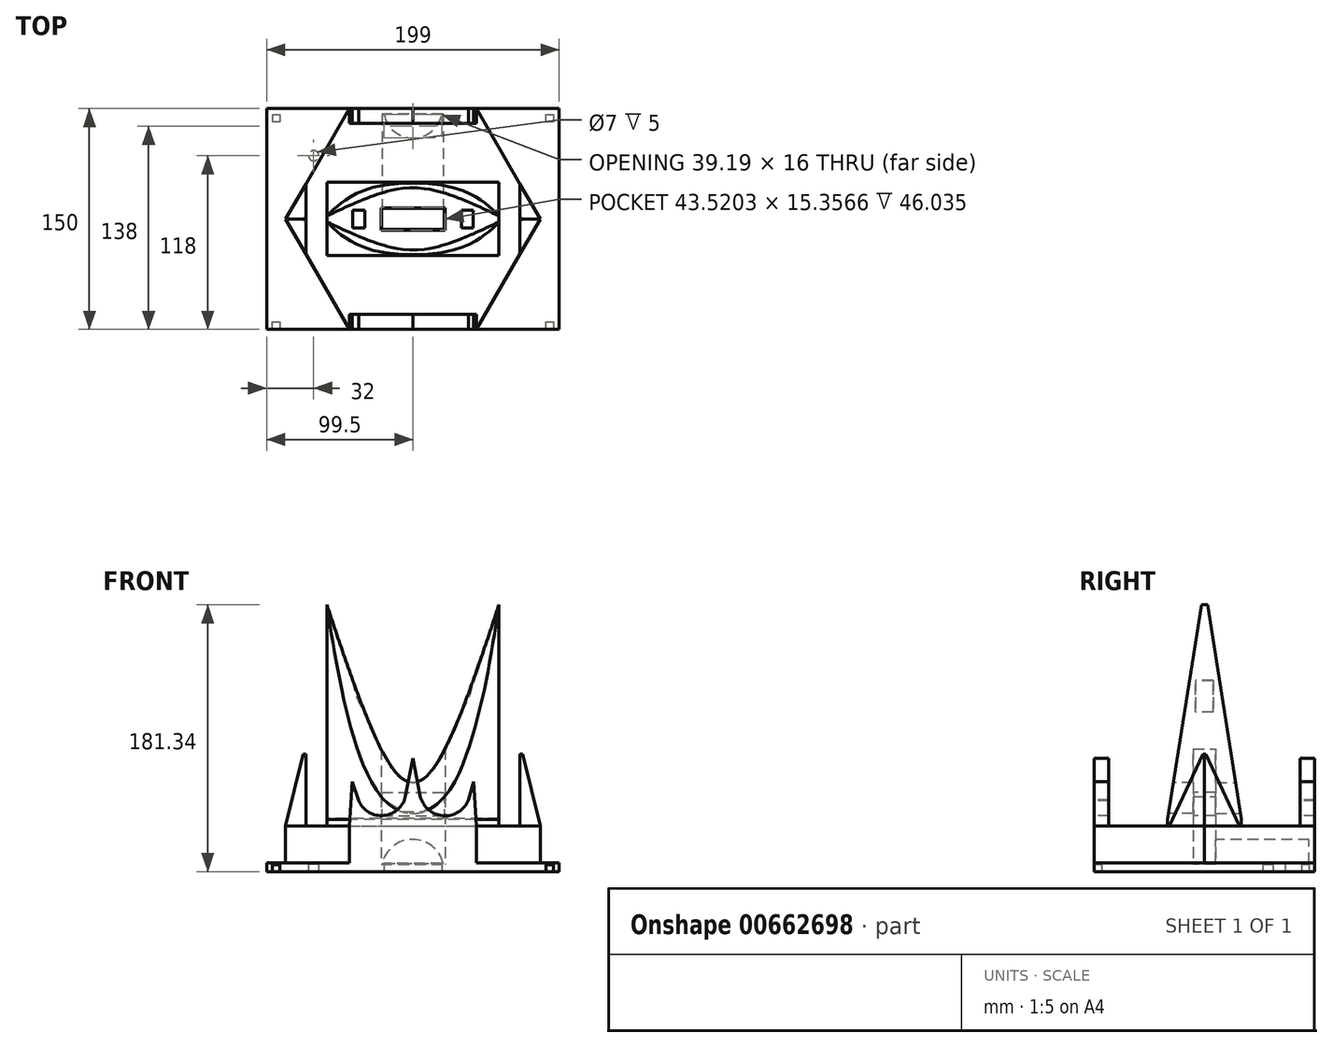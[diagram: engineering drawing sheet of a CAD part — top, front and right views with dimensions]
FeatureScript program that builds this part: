
annotation { "Feature Type Name" : "Feature", "Feature Type Description" : "" }
export const myFeature = defineFeature(function(context is Context, id is Id, definition is map)
    precondition{}
    {
        {
            var Q0;
            Q0=qCreatedBy(makeId("Top.planeOp"),FACE);
            var sketch = newSketch(context, id + "F0", { "sketchPlane" : qUnion([Q0])});
            skLineSegment(sketch, "E0.bottom", {"start": v(-99.5, 75) * mm, "end": v(99.5, 75) * mm});
            skLineSegment(sketch, "E0.left", {"start": v(-99.5, 75) * mm, "end": v(-99.5, -75) * mm});
            skLineSegment(sketch, "E0.right", {"start": v(99.5, 75) * mm, "end": v(99.5, -75) * mm});
            skPoint(sketch, "E0.middle", {"position": v(0, 0) * mm});
            skLineSegment(sketch, "E1.1", {"start": v(-95.5, 71) * mm, "end": v(-95.5, -70) * mm});
            skLineSegment(sketch, "E1.2", {"start": v(-95.5, 71) * mm, "end": v(95.4, 71) * mm});
            skLineSegment(sketch, "E1.3", {"start": v(95.4, 71) * mm, "end": v(95.4, -70) * mm});
            skLineSegment(sketch, "E2", {"start": v(0, -75) * mm, "end": v(0, -73) * mm});
            skPoint(sketch, "E2.endSnap0", {"position": v(0, -75) * mm});
            skPoint(sketch, "E3.end.orphan", {"position": v(95.5, 0) * mm});
            skLineSegment(sketch, "E4", {"start": v(-99.5, -75) * mm, "end": v(-95.5, -75) * mm});
            skLineSegment(sketch, "E5", {"start": v(-95.5, -75) * mm, "end": v(-95.5, -70) * mm});
            skLineSegment(sketch, "E6", {"start": v(95.4, -70) * mm, "end": v(95.4, -75) * mm});
            skLineSegment(sketch, "E7", {"start": v(95.4, -75) * mm, "end": v(99.5, -75) * mm});
            skPoint(sketch, "E8.end.orphan", {"position": v(-95.5, -70) * mm});
            skLineSegment(sketch, "E9", {"start": v(-90.5, 71) * mm, "end": v(-90.5, 66) * mm});
            skLineSegment(sketch, "E10", {"start": v(-90.5, 66) * mm, "end": v(-95.5, 66) * mm});
            skLineSegment(sketch, "E11", {"start": v(95.4, 66) * mm, "end": v(90.4, 66) * mm});
            skLineSegment(sketch, "E12", {"start": v(90.4, 66) * mm, "end": v(90.4, 71) * mm});
            skLineSegment(sketch, "E13", {"start": v(-95.5, 71) * mm, "end": v(-90.5, 71) * mm});
            skLineSegment(sketch, "E14", {"start": v(-95.5, 71) * mm, "end": v(-95.5, 66) * mm});
            skLineSegment(sketch, "E15", {"start": v(90.4, 71) * mm, "end": v(95.4, 71) * mm});
            skLineSegment(sketch, "E16", {"start": v(95.4, 66) * mm, "end": v(95.4, 71) * mm});
            skLineSegment(sketch, "E17", {"start": v(95.4, -75) * mm, "end": v(90.4, -75) * mm});
            skLineSegment(sketch, "E18", {"start": v(90.4, -75) * mm, "end": v(90.4, -70) * mm});
            skLineSegment(sketch, "E19", {"start": v(90.4, -70) * mm, "end": v(95.4, -70) * mm});
            skLineSegment(sketch, "E20", {"start": v(-95.5, -70) * mm, "end": v(-90.5, -70) * mm});
            skLineSegment(sketch, "E21", {"start": v(-95.5, -75) * mm, "end": v(-90.5, -75) * mm});
            skLineSegment(sketch, "E22", {"start": v(-90.5, -70) * mm, "end": v(-90.5, -75) * mm});
            skLineSegment(sketch, "E23", {"start": v(0, 73) * mm, "end": v(0, 71) * mm});
            skPoint(sketch, "E24.MirrorCS.end.orphan", {"position": v(-8.62, 71) * mm});
            skPoint(sketch, "E24.MirrorCS.start.orphan", {"position": v(8.62, 71) * mm});
            skSolve(sketch);
        }
        {
            var Q0;
            Q0=qCreatedBy(makeId("Top.planeOp"),FACE);
            var sketch = newSketch(context, id + "F1", { "sketchPlane" : qUnion([Q0])});
            skLineSegment(sketch, "E25.bottom", {"start": v(-99.5, 75) * mm, "end": v(-20, 75) * mm});
            skLineSegment(sketch, "E25.top", {"start": v(-99.5, -75) * mm, "end": v(99.5, -75) * mm});
            skLineSegment(sketch, "E25.left", {"start": v(-99.5, 75) * mm, "end": v(-99.5, -75) * mm});
            skLineSegment(sketch, "E25.right", {"start": v(99.5, 75) * mm, "end": v(99.5, -75) * mm});
            skPoint(sketch, "E25.middle", {"position": v(0, 0) * mm});
            skCircle(sketch, "E26", {"center": v(-67.5, 43) * mm, "radius": 3.5 * mm});
            skLineSegment(sketch, "E27.trimOffspring", {"start": v(20, 75) * mm, "end": v(99.5, 75) * mm});
            skArc(sketch, "E28", {"start": v(-20, 75) * mm, "mid": v(0, 55) * mm, "end": v(20, 75) * mm});
            skLineSegment(sketch, "E29", {"start": v(-20, 75) * mm, "end": v(20, 75) * mm});
            skLineSegment(sketch, "E30", {"start": v(19.6, 71) * mm, "end": v(-19.6, 71) * mm});
            skLineSegment(sketch, "E31", {"start": v(-67.5, 43) * mm, "end": v(-67.5, 75) * mm});
            skLineSegment(sketch, "E32", {"start": v(-67.5, 43) * mm, "end": v(-99.5, 43) * mm});
            skSolve(sketch);
        }
        {
            var Q0;
            Q0=qSketchRegion(id+"F1",true);
            extrude(context, id + "F2", {"entities" : qUnion([Q0]), "depth" : 6 * mm, "offsetDistance" : 25 * mm});
        }
        {
            var Q0;
            Q0=makeQuery(id+"F0.imprint","IMPRINT",FACE,{"disambiguationData":[TD([[makeQuery(id+"F0.imprint","IMPRINT",EDGE,{"derivedFrom":sQuery(id+"F0.wireOp",EDGE,"E9")}),-1.0]])]});
            var Q1;
            Q1=makeQuery(id+"F0.imprint","IMPRINT",FACE,{"disambiguationData":[TD([[makeQuery(id+"F0.imprint","IMPRINT",EDGE,{"derivedFrom":sQuery(id+"F0.wireOp",EDGE,"E11")}),-1.0]])]});
            var Q2;
            Q2=makeQuery(id+"F0.imprint","IMPRINT",FACE,{"disambiguationData":[TD([[makeQuery(id+"F0.imprint","IMPRINT",EDGE,{"derivedFrom":sQuery(id+"F0.wireOp",EDGE,"E5")}),-1.0]])]});
            var Q3;
            Q3=makeQuery(id+"F0.imprint","IMPRINT",FACE,{"disambiguationData":[TD([[makeQuery(id+"F0.imprint","IMPRINT",EDGE,{"derivedFrom":sQuery(id+"F0.wireOp",EDGE,"E6")}),-1.0]])]});
            extrude(context, id + "F3", {"entities" : qUnion([Q0, Q1, Q2, Q3]), "operationType" : NewBodyOperationType.REMOVE, "depth" : 4.5 * mm, "offsetDistance" : 25 * mm});
        }
        {
            var Q0;
            Q0=makeQuery(id+"F2.opExtrude","CAP_FACE",FACE,{"disambiguationData":[OSD([sQuery(id+"F1.wireOp",EDGE,"E25.bottom"),sQuery(id+"F1.wireOp",EDGE,"E25.top"),sQuery(id+"F1.wireOp",EDGE,"E25.left"),sQuery(id+"F1.wireOp",EDGE,"E25.right"),sQuery(id+"F1.wireOp",EDGE,"E26"),sQuery(id+"F1.wireOp",EDGE,"E27.trimOffspring"),sQuery(id+"F1.wireOp",EDGE,"E28")])],"isStart":false});
            var sketch = newSketch(context, id + "F4", { "sketchPlane" : qUnion([Q0])});
            skCircle(sketch, "E33.cCircle", {"center": v(0, 0) * mm, "radius": 75 * mm, "construction": true});
            skLineSegment(sketch, "E33.0", {"start": v(-43.3, 75) * mm, "end": v(43.3, 75) * mm});
            skLineSegment(sketch, "E33.1", {"start": v(43.3, 75) * mm, "end": v(86.6, 0) * mm});
            skLineSegment(sketch, "E33.2", {"start": v(86.6, 0) * mm, "end": v(43.3, -75) * mm});
            skLineSegment(sketch, "E33.3", {"start": v(43.3, -75) * mm, "end": v(-43.3, -75) * mm});
            skLineSegment(sketch, "E33.4", {"start": v(-43.3, -75) * mm, "end": v(-86.6, 0) * mm});
            skLineSegment(sketch, "E33.5", {"start": v(-86.6, 0) * mm, "end": v(-43.3, 75) * mm});
            skPoint(sketch, "E33.0.midPoint", {"position": v(0, 75) * mm});
            skCircle(sketch, "E34", {"center": v(-67.5, 43) * mm, "radius": 3.84 * mm});
            skSolve(sketch);
        }
        {
            var Q0;
            Q0=makeQuery(id+"F4.imprint","IMPRINT",FACE,{"disambiguationData":[TD([[makeQuery(id+"F4.imprint","IMPRINT",EDGE,{"derivedFrom":makeQuery(id+"F2.opExtrude","CAP_EDGE",EDGE,{"disambiguationData":[OSD([sQuery(id+"F1.wireOp",EDGE,"E26")])],"isStart":false})}),1.0]])]});
            extrude(context, id + "F5", {"entities" : qUnion([Q0]), "operationType" : NewBodyOperationType.ADD, "oppositeDirection" : true, "depth" : 1 * mm, "offsetDistance" : 25 * mm});
        }
        {
            var Q0;
            {var subQ0=sQuery(id+"F4.wireOp",EDGE,"E33.1");Q0=makeQuery(id+"F4.imprint","IMPRINT",FACE,{"disambiguationData":[TD([[makeQuery(id+"F4.imprint","IMPRINT",EDGE,{"derivedFrom":subQ0}),-1.0]])]});}
            var Q1;
            {var subQ1=makeQuery(id+"F2.opExtrude","CAP_EDGE",EDGE,{"disambiguationData":[OSD([sQuery(id+"F1.wireOp",EDGE,"E28")])],"isStart":false});Q1=makeQuery(id+"F4.imprint","IMPRINT",FACE,{"disambiguationData":[TD([[makeQuery(id+"F4.imprint","IMPRINT",EDGE,{"derivedFrom":subQ1}),1.0]])]});}
            extrude(context, id + "F6", {"entities" : qUnion([Q0, Q1]), "operationType" : NewBodyOperationType.ADD, "depth" : 25 * mm, "offsetDistance" : 25 * mm});
        }
        {
            var Q0;
            Q0=makeQuery(id+"F6.boolean.opBoolean","MERGE",FACE,{"derivedFrom":[makeQuery(id+"F2.opExtrude","SWEPT_FACE",FACE,{"disambiguationData":[OSD([sQuery(id+"F1.wireOp",EDGE,"E25.top")])]}),makeQuery(id+"F6.opExtrude","SWEPT_FACE",FACE,{"disambiguationData":[OSD([sQuery(id+"F4.wireOp",EDGE,"E33.3")])]})]});
            var sketch = newSketch(context, id + "F7", { "sketchPlane" : qUnion([Q0])});
            skLineSegment(sketch, "E35", {"start": v(-43.3, 31) * mm, "end": v(43.3, 31) * mm});
            skLineSegment(sketch, "E36", {"start": v(-41.3, 61) * mm, "end": v(-43.3, 31) * mm});
            skLineSegment(sketch, "E37", {"start": v(-36.89, 48.16) * mm, "end": v(-41.3, 61) * mm});
            skLineSegment(sketch, "E38", {"start": v(4.9, 51.85) * mm, "end": v(-0.01, 77) * mm});
            skLineSegment(sketch, "E39", {"start": v(-4.94, 51.67) * mm, "end": v(-0.01, 77) * mm});
            skLineSegment(sketch, "E40", {"start": v(41.3, 61) * mm, "end": v(37.86, 48.79) * mm});
            skLineSegment(sketch, "E41", {"start": v(43.3, 31) * mm, "end": v(41.3, 61) * mm});
            skArc(sketch, "E42", {"start": v(-36.89, 48.16) * mm, "mid": v(-19.62, 38.15) * mm, "end": v(-4.94, 51.67) * mm});
            skArc(sketch, "E43", {"start": v(4.9, 51.85) * mm, "mid": v(20.24, 37.98) * mm, "end": v(37.86, 48.79) * mm});
            skSolve(sketch);
        }
        {
            var Q0;
            Q0=makeQuery(id+"F7.imprint","IMPRINT",FACE,{"disambiguationData":[TD([[makeQuery(id+"F7.imprint","IMPRINT",EDGE,{"derivedFrom":sQuery(id+"F7.wireOp",EDGE,"E35")}),1.0]])]});
            extrude(context, id + "F8", {"entities" : qUnion([Q0]), "operationType" : NewBodyOperationType.ADD, "oppositeDirection" : true, "depth" : 10 * mm, "offsetDistance" : 25 * mm});
        }
        {
            var Q0;
            {var subQ0=sQuery(id+"F4.wireOp",EDGE,"E33.1");var subQ1=sQuery(id+"F4.wireOp",EDGE,"E33.0");var subQ3=sQuery(id+"F4.wireOp",EDGE,"E33.2");var subQ4=sQuery(id+"F4.wireOp",EDGE,"E33.3");Q0=makeQuery(id+"F8.boolean.opBoolean","SPLIT",FACE,{"disambiguationData":[TD([makeQuery(id+"F6.opExtrude","SWEPT_FACE",FACE,{"disambiguationData":[OSD([subQ0])]})])],"derivedFrom":makeQuery(id+"F6.opExtrude","CAP_FACE",FACE,{"disambiguationData":[OSD([subQ1,subQ0,subQ3,subQ4,sQuery(id+"F4.wireOp",EDGE,"E33.4"),sQuery(id+"F4.wireOp",EDGE,"E33.5")])],"isStart":false})});}
            var sketch = newSketch(context, id + "F9", { "sketchPlane" : qUnion([Q0])});
            skLineSegment(sketch, "E44", {"start": v(86.6, 0) * mm, "end": v(72.84, 23.84) * mm});
            skLineSegment(sketch, "E45", {"start": v(72.84, 23.84) * mm, "end": v(72.84, -23.84) * mm});
            skLineSegment(sketch, "E46", {"start": v(72.84, -23.84) * mm, "end": v(86.6, 0) * mm});
            skLineSegment(sketch, "E47.MirrorCS", {"start": v(-72.84, 23.84) * mm, "end": v(-72.84, -23.84) * mm});
            skLineSegment(sketch, "E48.MirrorCS", {"start": v(-86.6, 0) * mm, "end": v(-72.84, 23.84) * mm});
            skLineSegment(sketch, "E49.MirrorCS", {"start": v(-72.84, -23.84) * mm, "end": v(-86.6, 0) * mm});
            skSolve(sketch);
        }
        {
            var Q0;
            Q0=qCreatedBy(makeId("Top.planeOp"),FACE);
            cPlane(context, id + "F10", {"entities" : qUnion([Q0]), "cplaneType" : CPlaneType.OFFSET, "offset" : 80 * mm, "width" : 150 * mm, "height" : 150 * mm});
        }
        {
            var Q0;
            Q0=qCreatedBy(id+"F10.planeOp",FACE);
            var sketch = newSketch(context, id + "F11", { "sketchPlane" : qUnion([Q0])});
            skLineSegment(sketch, "E50", {"start": v(-74.52, 0) * mm, "end": v(-72.84, 1.05) * mm});
            skLineSegment(sketch, "E51", {"start": v(-72.84, 1.05) * mm, "end": v(-72.84, -0.99) * mm});
            skLineSegment(sketch, "E52", {"start": v(-72.84, -0.99) * mm, "end": v(-74.52, 0) * mm});
            skLineSegment(sketch, "E53.MirrorCS", {"start": v(74.52, 0) * mm, "end": v(72.84, 1.05) * mm});
            skLineSegment(sketch, "E54.MirrorCS", {"start": v(72.84, 1.05) * mm, "end": v(72.84, -0.99) * mm});
            skLineSegment(sketch, "E55.MirrorCS", {"start": v(72.84, -0.99) * mm, "end": v(74.52, 0) * mm});
            skSolve(sketch);
        }
        {
            var Q1;
            Q1=makeQuery(id+"F9.imprint","IMPRINT",FACE,{"disambiguationData":[TD([[makeQuery(id+"F9.imprint","IMPRINT",EDGE,{"derivedFrom":sQuery(id+"F9.wireOp",EDGE,"E47.MirrorCS")}),-1.0]])]});
            var Q2;
            Q2=makeQuery(id+"F11.imprint","IMPRINT",FACE,{"disambiguationData":[TD([[makeQuery(id+"F11.imprint","IMPRINT",EDGE,{"derivedFrom":sQuery(id+"F11.wireOp",EDGE,"E50")}),-1.0]])]});
            loft(context, id + "F12", {"operationType" : NewBodyOperationType.ADD, "sheetProfilesArray" : [{ "sheetProfileEntities" : qUnion([Q1]) }, { "sheetProfileEntities" : qUnion([Q2]) }]});
        }
        {
            var Q1;
            Q1=makeQuery(id+"F9.imprint","IMPRINT",FACE,{"disambiguationData":[TD([[makeQuery(id+"F9.imprint","IMPRINT",EDGE,{"derivedFrom":sQuery(id+"F9.wireOp",EDGE,"E44")}),-1.0]])]});
            var Q2;
            Q2=makeQuery(id+"F11.imprint","IMPRINT",FACE,{"disambiguationData":[TD([[makeQuery(id+"F11.imprint","IMPRINT",EDGE,{"derivedFrom":sQuery(id+"F11.wireOp",EDGE,"E53.MirrorCS")}),1.0]])]});
            loft(context, id + "F13", {"operationType" : NewBodyOperationType.ADD, "sheetProfilesArray" : [{ "sheetProfileEntities" : qUnion([Q1]) }, { "sheetProfileEntities" : qUnion([Q2]) }]});
        }
        {
            var Q0;
            Q0=makeQuery(id+"F7.imprint","IMPRINT",FACE,{"disambiguationData":[TD([[makeQuery(id+"F7.imprint","IMPRINT",EDGE,{"derivedFrom":sQuery(id+"F7.wireOp",EDGE,"E35")}),1.0]])]});
            extrude(context, id + "F14", {"entities" : qUnion([Q0]), "operationType" : NewBodyOperationType.ADD, "oppositeDirection" : true, "depth" : 150 * mm, "offsetDistance" : 25 * mm, "hasSecondDirection" : true, "secondDirectionOppositeDirection" : true, "secondDirectionDepth" : 140 * mm});
        }
        {
            var Q0;
            Q0=qCreatedBy(makeId("Front.planeOp"),FACE);
            var sketch = newSketch(context, id + "F15", { "sketchPlane" : qUnion([Q0])});
            skLineSegment(sketch, "E56", {"start": v(-58.4, 30.78) * mm, "end": v(43.31, 30.78) * mm});
            skLineSegment(sketch, "E57", {"start": v(43.31, 30.78) * mm, "end": v(58.37, 30.78) * mm});
            skLineSegment(sketch, "E58", {"start": v(58.37, 30.78) * mm, "end": v(58.37, 181.34) * mm});
            skLineSegment(sketch, "E59", {"start": v(-58.4, 181.34) * mm, "end": v(-58.4, 30.78) * mm});
            skFitSpline(sketch, "E60", {"points": [v(-58.4, 181.34) * mm, v(0, 60.63) * mm, v(58.37, 181.34) * mm], "startDerivative": vector(188.08, -575.5) * mm, "endDerivative": vector(187.8, 577.3) * mm});
            skFitSpline(sketch, "E61", {"points": [v(-58.4, 181.34) * mm, v(0, 39.61) * mm, v(58.37, 181.34) * mm], "startDerivative": vector(103.86, -722.6) * mm, "endDerivative": vector(101.23, 721.58) * mm});
            skArc(sketch, "E62", {"start": v(-40.88, 130) * mm, "mid": v(-38.35, 118.63) * mm, "end": v(-32.74, 108.44) * mm});
            skArc(sketch, "E63.trimOffspring", {"start": v(32.87, 108.61) * mm, "mid": v(38.37, 118.67) * mm, "end": v(40.87, 129.86) * mm});
            skSolve(sketch);
        }
        {
            var Q0;
            Q0=makeQuery(id+"F15.imprint","IMPRINT",FACE,{"disambiguationData":[TD([[makeQuery(id+"F15.imprint","IMPRINT",EDGE,{"derivedFrom":sQuery(id+"F15.wireOp",EDGE,"E56")}),1.0]])]});
            extrude(context, id + "F16", {"entities" : qUnion([Q0]), "operationType" : NewBodyOperationType.ADD, "depth" : 25 * mm, "offsetDistance" : 25 * mm, "hasSecondDirection" : true, "secondDirectionOppositeDirection" : true, "secondDirectionDepth" : 25 * mm});
        }
        {
            var Q0;
            {var subQ0=sQuery(id+"F15.wireOp",EDGE,"E61");Q0=makeQuery(id+"F15.imprint","IMPRINT",FACE,{"disambiguationData":[TD([[makeQuery(id+"F15.imprint","IMPRINT",EDGE,{"derivedFrom":subQ0}),1.0]])]});}
            var Q1;
            {var subQ0=sQuery(id+"F15.wireOp",EDGE,"E62");Q1=makeQuery(id+"F15.imprint","IMPRINT",FACE,{"disambiguationData":[TD([[makeQuery(id+"F15.imprint","IMPRINT",EDGE,{"derivedFrom":subQ0}),1.0]])]});}
            var Q2;
            {var subQ0=sQuery(id+"F15.wireOp",EDGE,"E63.trimOffspring");Q2=makeQuery(id+"F15.imprint","IMPRINT",FACE,{"disambiguationData":[TD([[makeQuery(id+"F15.imprint","IMPRINT",EDGE,{"derivedFrom":subQ0}),1.0]])]});}
            extrude(context, id + "F17", {"entities" : qUnion([Q0, Q1, Q2]), "depth" : 25 * mm, "offsetDistance" : 25 * mm, "hasSecondDirection" : true, "secondDirectionOppositeDirection" : true, "secondDirectionDepth" : 25 * mm});
        }
        {
            var Q0;
            Q0=qCreatedBy(makeId("Right.planeOp"),FACE);
            var sketch = newSketch(context, id + "F18", { "sketchPlane" : qUnion([Q0])});
            skLineSegment(sketch, "E64", {"start": v(0, 181.61) * mm, "end": v(2, 181.61) * mm});
            skLineSegment(sketch, "E65", {"start": v(2, 181.61) * mm, "end": v(-2, 181.61) * mm});
            skLineSegment(sketch, "E66", {"start": v(-2, 181.61) * mm, "end": v(-25.53, 31.98) * mm});
            skLineSegment(sketch, "E67", {"start": v(-25.53, 31.98) * mm, "end": v(-25.53, 188.45) * mm});
            skLineSegment(sketch, "E68", {"start": v(-25.53, 188.45) * mm, "end": v(26.57, 188.45) * mm});
            skLineSegment(sketch, "E69", {"start": v(26.57, 188.45) * mm, "end": v(25.61, 32.2) * mm});
            skLineSegment(sketch, "E70", {"start": v(25.61, 32.2) * mm, "end": v(2, 181.61) * mm});
            skSolve(sketch);
        }
        {
            var Q0;
            {var subQ0=sQuery(id+"F18.wireOp",EDGE,"E66");Q0=makeQuery(id+"F18.imprint","IMPRINT",FACE,{"disambiguationData":[TD([[makeQuery(id+"F18.imprint","IMPRINT",EDGE,{"derivedFrom":subQ0}),-1.0]])]});}
            extrude(context, id + "F19", {"entities" : qUnion([Q0]), "operationType" : NewBodyOperationType.REMOVE, "oppositeDirection" : true, "depth" : 60 * mm, "offsetDistance" : 25 * mm, "hasSecondDirection" : true, "secondDirectionOppositeDirection" : false, "secondDirectionDepth" : 60 * mm});
        }
        {
            var Q0;
            Q0=qCreatedBy(makeId("Top.planeOp"),FACE);
            var sketch = newSketch(context, id + "F20", { "sketchPlane" : qUnion([Q0])});
            skPoint(sketch, "E71.firstSnap0", {"position": v(0, 7.68) * mm});
            skPoint(sketch, "E71.firstSnap1", {"position": v(-21.7, 0) * mm});
            skPoint(sketch, "E71.oppositeSnap0", {"position": v(0, -7.68) * mm});
            skLineSegment(sketch, "E71.bottom", {"start": v(-21.7, 7.68) * mm, "end": v(21.81, 7.68) * mm});
            skLineSegment(sketch, "E71.top", {"start": v(-21.7, -7.68) * mm, "end": v(21.81, -7.68) * mm});
            skLineSegment(sketch, "E71.left", {"start": v(-21.7, 7.68) * mm, "end": v(-21.7, -7.68) * mm});
            skLineSegment(sketch, "E71.right", {"start": v(21.81, 7.68) * mm, "end": v(21.81, -7.68) * mm});
            skLineSegment(sketch, "E72.bottom", {"start": v(-21.27, 7.32) * mm, "end": v(21.26, 7.32) * mm});
            skLineSegment(sketch, "E72.top", {"start": v(-21.27, -7.18) * mm, "end": v(21.26, -7.18) * mm});
            skLineSegment(sketch, "E72.left", {"start": v(-21.27, 7.32) * mm, "end": v(-21.27, -7.18) * mm});
            skLineSegment(sketch, "E72.right", {"start": v(21.26, 7.32) * mm, "end": v(21.26, -7.18) * mm});
            skSolve(sketch);
        }
        {
            var Q0;
            Q0 = qSketchRegion(id + "F20", true);
            var Q1;
            Q1=makeQuery(id+"F20.imprint","IMPRINT",FACE,{"disambiguationData":[TD([[makeQuery(id+"F20.imprint","IMPRINT",EDGE,{"derivedFrom":sQuery(id+"F20.wireOp",EDGE,"E72.bottom")}),-1.0]])]});
            extrude(context, id + "F21", {"entities" : qUnion([Q0, Q1]), "operationType" : NewBodyOperationType.REMOVE, "depth" : 100 * mm, "offsetDistance" : 25 * mm, "hasSecondDirection" : true, "secondDirectionOppositeDirection" : false, "secondDirectionDepth" : 5 * mm});
        }
        {
            var Q0;
            Q0=qCreatedBy(makeId("Front.planeOp"),FACE);
            var sketch = newSketch(context, id + "F22", { "sketchPlane" : qUnion([Q0])});
            skLineSegment(sketch, "E73.top", {"start": v(20.6, 5.53) * mm, "end": v(-20.98, 5.53) * mm});
            skArc(sketch, "E74", {"start": v(20.6, 5.53) * mm, "mid": v(-0.19, 21.9) * mm, "end": v(-20.98, 5.53) * mm});
            skSolve(sketch);
        }
        {
            var Q0;
            Q0 = qSketchRegion(id + "F22", true);
            extrude(context, id + "F23", {"entities" : qUnion([Q0]), "operationType" : NewBodyOperationType.REMOVE, "oppositeDirection" : true, "depth" : 71.2 * mm, "offsetDistance" : 25 * mm, "hasSecondDirection" : true, "secondDirectionOppositeDirection" : false, "secondDirectionDepth" : 7.5 * mm});
        }
        {
            var Q0;
            Q0=makeQuery(id+"F20.imprint","IMPRINT",FACE,{"disambiguationData":[TD([[makeQuery(id+"F20.imprint","IMPRINT",EDGE,{"derivedFrom":sQuery(id+"F20.wireOp",EDGE,"E72.bottom")}),-1.0]])]});
            extrude(context, id + "F24", {"entities" : qUnion([Q0]), "operationType" : NewBodyOperationType.ADD, "depth" : 54 * mm, "offsetDistance" : 25 * mm, "hasSecondDirection" : true, "secondDirectionOppositeDirection" : false, "secondDirectionDepth" : 38 * mm});
        }
        {
            var Q0;
            {var subQ0=sQuery(id+"F15.wireOp",EDGE,"E62");Q0=makeQuery(id+"F15.imprint","IMPRINT",FACE,{"disambiguationData":[TD([[makeQuery(id+"F15.imprint","IMPRINT",EDGE,{"derivedFrom":subQ0}),1.0]])]});}
            var Q1;
            {var subQ0=sQuery(id+"F15.wireOp",EDGE,"E63.trimOffspring");Q1=makeQuery(id+"F15.imprint","IMPRINT",FACE,{"disambiguationData":[TD([[makeQuery(id+"F15.imprint","IMPRINT",EDGE,{"derivedFrom":subQ0}),1.0]])]});}
            extrude(context, id + "F25", {"entities" : qUnion([Q0, Q1]), "operationType" : NewBodyOperationType.REMOVE, "oppositeDirection" : true, "depth" : 6 * mm, "offsetDistance" : 25 * mm, "hasSecondDirection" : true, "secondDirectionOppositeDirection" : false, "secondDirectionDepth" : 6 * mm});
        }
    });
